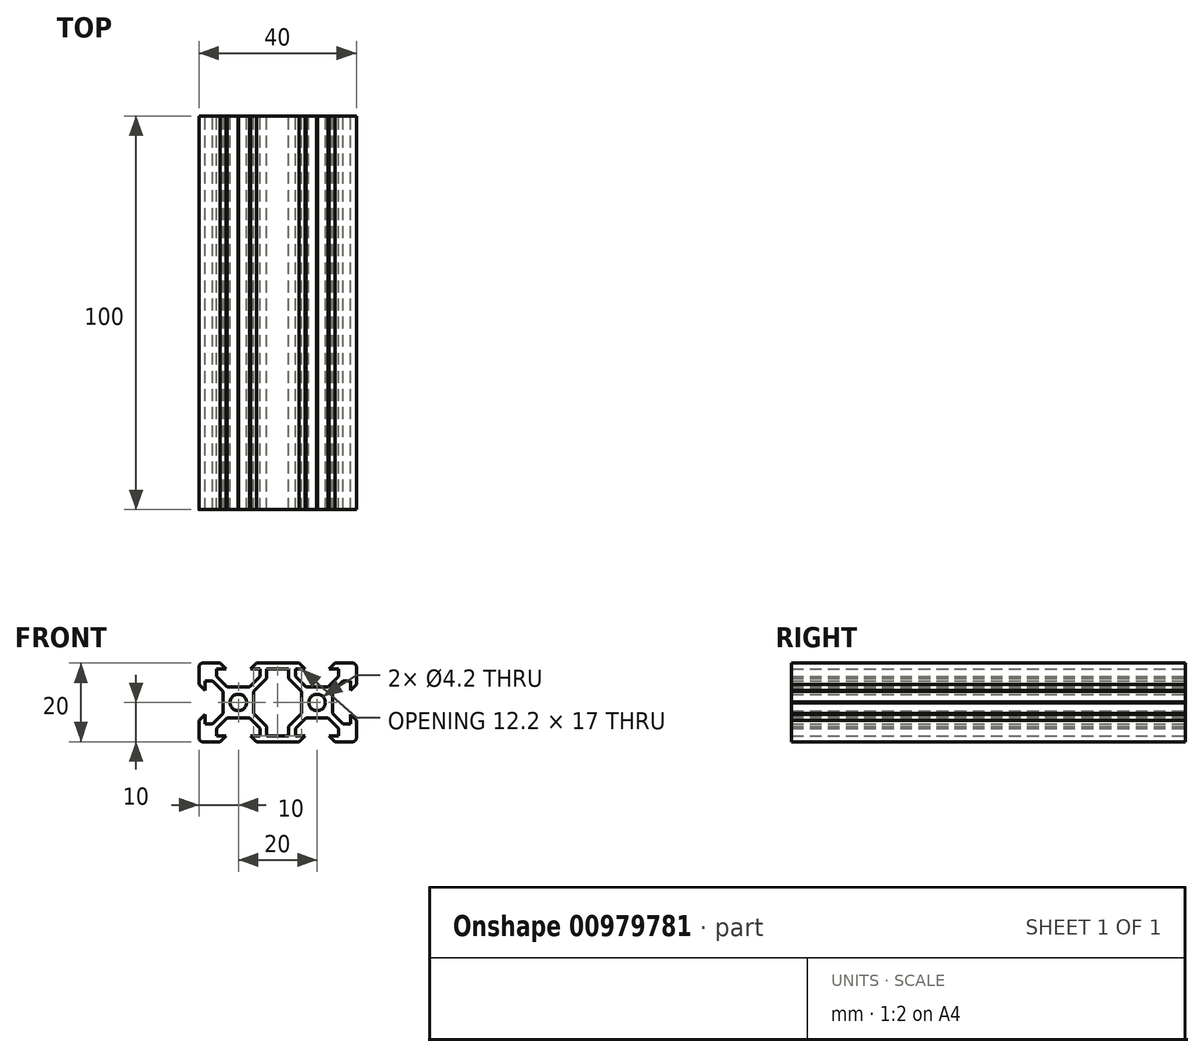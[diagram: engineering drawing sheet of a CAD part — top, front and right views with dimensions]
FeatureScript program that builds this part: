
annotation { "Feature Type Name" : "Feature", "Feature Type Description" : "" }
export const myFeature = defineFeature(function(context is Context, id is Id, definition is map)
    precondition{}
    {
        {
            var Q0;
            Q0=qCreatedBy(makeId("Front.planeOp"),FACE);
            var sketch = newSketch(context, id + "F0", { "sketchPlane" : qUnion([Q0])});
            skLineSegment(sketch, "E0.MirrorCS", {"start": v(-15.5, 8.5) * mm, "end": v(-15.5, 6.56) * mm});
            skLineSegment(sketch, "E1.MirrorCS", {"start": v(-16.56, 5.5) * mm, "end": v(-18.5, 5.5) * mm});
            skLineSegment(sketch, "E2.MirrorCS", {"start": v(-20, 10) * mm, "end": v(-20, 4.6) * mm});
            skLineSegment(sketch, "E3.MirrorCS", {"start": v(-2.8, 6.14) * mm, "end": v(-6.1, 2.84) * mm});
            skLineSegment(sketch, "E4.MirrorCS", {"start": v(-6.1, 2.84) * mm, "end": v(-6.1, 0) * mm});
            skLineSegment(sketch, "E5.MirrorCS", {"start": v(-18.5, 3.1) * mm, "end": v(-20, 4.6) * mm});
            skLineSegment(sketch, "E6.MirrorCS", {"start": v(-15.5, 6.56) * mm, "end": v(-12.84, 3.9) * mm});
            skLineSegment(sketch, "E7.MirrorCS", {"start": v(-13.1, 8.5) * mm, "end": v(-14.6, 10) * mm});
            skLineSegment(sketch, "E8.MirrorCS", {"start": v(-4.5, 8.5) * mm, "end": v(-4.5, 6.56) * mm});
            skLineSegment(sketch, "E9.MirrorCS", {"start": v(-18.5, 5.5) * mm, "end": v(-18.5, 3.1) * mm});
            skLineSegment(sketch, "E10.MirrorCS", {"start": v(-4.5, 6.56) * mm, "end": v(-7.16, 3.9) * mm});
            skLineSegment(sketch, "E11.MirrorCS", {"start": v(-13.9, 2.84) * mm, "end": v(-13.9, 0.1) * mm});
            skLineSegment(sketch, "E12.MirrorCS", {"start": v(-6.9, 8.5) * mm, "end": v(-5.4, 10) * mm});
            skLineSegment(sketch, "E13.MirrorCS", {"start": v(-5.4, 10) * mm, "end": v(0, 10) * mm});
            skLineSegment(sketch, "E14.MirrorCS", {"start": v(-4.5, 8.5) * mm, "end": v(-6.9, 8.5) * mm});
            skLineSegment(sketch, "E15.MirrorCS", {"start": v(-14.6, 10) * mm, "end": v(-20, 10) * mm});
            skLineSegment(sketch, "E16.MirrorCS", {"start": v(-16.56, 5.5) * mm, "end": v(-13.9, 2.84) * mm});
            skLineSegment(sketch, "E17.MirrorCS", {"start": v(-15.5, 8.5) * mm, "end": v(-13.1, 8.5) * mm});
            skLineSegment(sketch, "E18", {"start": v(-2.8, 8.5) * mm, "end": v(-2.8, 6.14) * mm});
            skLineSegment(sketch, "E19", {"start": v(-12.84, 3.9) * mm, "end": v(-10.1, 3.9) * mm});
            skLineSegment(sketch, "E20", {"start": v(-2.8, 8.5) * mm, "end": v(0, 8.5) * mm});
            skLineSegment(sketch, "E21", {"start": v(-12.25, 8.5) * mm, "end": v(-7.9, 8.5) * mm, "construction": true});
            skLineSegment(sketch, "E22", {"start": v(-7.9, 10) * mm, "end": v(-12.25, 10) * mm, "construction": true});
            skArc(sketch, "E23", {"start": v(-7.9, 0) * mm, "mid": v(-10, 2.1) * mm, "end": v(-12.1, 0) * mm});
            skLineSegment(sketch, "E24", {"start": v(-10, 0) * mm, "end": v(-10, 1.07) * mm, "construction": true});
            skLineSegment(sketch, "E25.MirrorCS", {"start": v(-10, 0) * mm, "end": v(-10, -1.07) * mm, "construction": true});
            skLineSegment(sketch, "E26.top", {"start": v(-10.1, 3.7) * mm, "end": v(-9.9, 3.7) * mm});
            skLineSegment(sketch, "E26.left", {"start": v(-10.1, 3.9) * mm, "end": v(-10.1, 3.7) * mm});
            skLineSegment(sketch, "E26.right", {"start": v(-9.9, 3.9) * mm, "end": v(-9.9, 3.7) * mm});
            skLineSegment(sketch, "E27.trimOffspring", {"start": v(-9.9, 3.9) * mm, "end": v(-7.16, 3.9) * mm});
            skLineSegment(sketch, "E28", {"start": v(-13.9, 0.1) * mm, "end": v(-13.7, 0.1) * mm});
            skLineSegment(sketch, "E29", {"start": v(-13.7, 0.1) * mm, "end": v(-13.7, 0) * mm});
            skPoint(sketch, "E30.orphan", {"position": v(-13.9, 0) * mm});
            skLineSegment(sketch, "E31.MirrorCS", {"start": v(13.7, 0.1) * mm, "end": v(13.7, 0) * mm});
            skLineSegment(sketch, "E32.MirrorCS", {"start": v(13.9, 0.1) * mm, "end": v(13.7, 0.1) * mm});
            skLineSegment(sketch, "E33.MirrorCS", {"start": v(10.1, 3.7) * mm, "end": v(9.9, 3.7) * mm});
            skLineSegment(sketch, "E34.MirrorCS", {"start": v(10.1, 3.9) * mm, "end": v(10.1, 3.7) * mm});
            skLineSegment(sketch, "E35.MirrorCS", {"start": v(9.9, 3.9) * mm, "end": v(9.9, 3.7) * mm});
            skLineSegment(sketch, "E36.MirrorCS", {"start": v(20, 10) * mm, "end": v(20, 4.6) * mm});
            skLineSegment(sketch, "E37.MirrorCS", {"start": v(4.5, 6.56) * mm, "end": v(7.16, 3.9) * mm});
            skLineSegment(sketch, "E38.MirrorCS", {"start": v(2.8, 8.5) * mm, "end": v(0, 8.5) * mm});
            skLineSegment(sketch, "E39.MirrorCS", {"start": v(18.5, 5.5) * mm, "end": v(18.5, 3.1) * mm});
            skLineSegment(sketch, "E40.MirrorCS", {"start": v(16.56, 5.5) * mm, "end": v(18.5, 5.5) * mm});
            skLineSegment(sketch, "E41.MirrorCS", {"start": v(15.5, 8.5) * mm, "end": v(15.5, 6.56) * mm});
            skLineSegment(sketch, "E42.MirrorCS", {"start": v(9.9, 3.9) * mm, "end": v(7.16, 3.9) * mm});
            skLineSegment(sketch, "E43.MirrorCS", {"start": v(13.9, 2.84) * mm, "end": v(13.9, 0.1) * mm});
            skLineSegment(sketch, "E44.MirrorCS", {"start": v(15.5, 8.5) * mm, "end": v(13.1, 8.5) * mm});
            skLineSegment(sketch, "E45.MirrorCS", {"start": v(16.56, 5.5) * mm, "end": v(13.9, 2.84) * mm});
            skLineSegment(sketch, "E46.MirrorCS", {"start": v(13.1, 8.5) * mm, "end": v(14.6, 10) * mm});
            skLineSegment(sketch, "E47.MirrorCS", {"start": v(15.5, 6.56) * mm, "end": v(12.84, 3.9) * mm});
            skLineSegment(sketch, "E48.MirrorCS", {"start": v(12.25, 8.5) * mm, "end": v(7.9, 8.5) * mm, "construction": true});
            skLineSegment(sketch, "E49.MirrorCS", {"start": v(12.84, 3.9) * mm, "end": v(10.1, 3.9) * mm});
            skLineSegment(sketch, "E50.MirrorCS", {"start": v(5.4, 10) * mm, "end": v(0, 10) * mm});
            skLineSegment(sketch, "E51.MirrorCS", {"start": v(2.8, 8.5) * mm, "end": v(2.8, 6.14) * mm});
            skLineSegment(sketch, "E52.MirrorCS", {"start": v(4.5, 8.5) * mm, "end": v(4.5, 6.56) * mm});
            skLineSegment(sketch, "E53.MirrorCS", {"start": v(18.5, 3.1) * mm, "end": v(20, 4.6) * mm});
            skPoint(sketch, "E54.MirrorP", {"position": v(13.9, 0) * mm});
            skArc(sketch, "E55.MirrorCS", {"start": v(7.9, 0) * mm, "mid": v(10, 2.1) * mm, "end": v(12.1, 0) * mm});
            skLineSegment(sketch, "E56.MirrorCS", {"start": v(6.1, 2.84) * mm, "end": v(6.1, 0) * mm});
            skLineSegment(sketch, "E57.MirrorCS", {"start": v(14.6, 10) * mm, "end": v(20, 10) * mm});
            skLineSegment(sketch, "E58.MirrorCS", {"start": v(10, 0) * mm, "end": v(10, 1.07) * mm, "construction": true});
            skLineSegment(sketch, "E59.MirrorCS", {"start": v(6.9, 8.5) * mm, "end": v(5.4, 10) * mm});
            skLineSegment(sketch, "E60.MirrorCS", {"start": v(2.8, 6.14) * mm, "end": v(6.1, 2.84) * mm});
            skLineSegment(sketch, "E61.MirrorCS", {"start": v(7.9, 10) * mm, "end": v(12.25, 10) * mm, "construction": true});
            skLineSegment(sketch, "E62.MirrorCS", {"start": v(4.5, 8.5) * mm, "end": v(6.9, 8.5) * mm});
            skLineSegment(sketch, "E63.MirrorCS", {"start": v(13.7, -0.1) * mm, "end": v(13.7, 0) * mm});
            skLineSegment(sketch, "E64.MirrorCS", {"start": v(-13.9, -0.1) * mm, "end": v(-13.7, -0.1) * mm});
            skLineSegment(sketch, "E65.MirrorCS", {"start": v(-13.7, -0.1) * mm, "end": v(-13.7, 0) * mm});
            skLineSegment(sketch, "E66.MirrorCS", {"start": v(13.9, -0.1) * mm, "end": v(13.7, -0.1) * mm});
            skLineSegment(sketch, "E67.MirrorCS", {"start": v(-9.9, -3.9) * mm, "end": v(-9.9, -3.7) * mm});
            skLineSegment(sketch, "E68.MirrorCS", {"start": v(9.9, -3.9) * mm, "end": v(9.9, -3.7) * mm});
            skLineSegment(sketch, "E69.MirrorCS", {"start": v(10.1, -3.9) * mm, "end": v(10.1, -3.7) * mm});
            skLineSegment(sketch, "E70.MirrorCS", {"start": v(10.1, -3.7) * mm, "end": v(9.9, -3.7) * mm});
            skLineSegment(sketch, "E71.MirrorCS", {"start": v(-10.1, -3.7) * mm, "end": v(-9.9, -3.7) * mm});
            skLineSegment(sketch, "E72.MirrorCS", {"start": v(-10.1, -3.9) * mm, "end": v(-10.1, -3.7) * mm});
            skLineSegment(sketch, "E73.MirrorCS", {"start": v(15.5, -6.56) * mm, "end": v(12.84, -3.9) * mm});
            skLineSegment(sketch, "E74.MirrorCS", {"start": v(-18.5, -3.1) * mm, "end": v(-20, -4.6) * mm});
            skLineSegment(sketch, "E75.MirrorCS", {"start": v(2.8, -6.14) * mm, "end": v(6.1, -2.84) * mm});
            skLineSegment(sketch, "E76.MirrorCS", {"start": v(-4.5, -8.5) * mm, "end": v(-6.9, -8.5) * mm});
            skLineSegment(sketch, "E77.MirrorCS", {"start": v(-6.9, -8.5) * mm, "end": v(-5.4, -10) * mm});
            skLineSegment(sketch, "E78.MirrorCS", {"start": v(-15.5, -8.5) * mm, "end": v(-13.1, -8.5) * mm});
            skLineSegment(sketch, "E79.MirrorCS", {"start": v(-12.25, -8.5) * mm, "end": v(-7.9, -8.5) * mm, "construction": true});
            skLineSegment(sketch, "E80.MirrorCS", {"start": v(13.9, -2.84) * mm, "end": v(13.9, -0.1) * mm});
            skLineSegment(sketch, "E81.MirrorCS", {"start": v(-15.5, -8.5) * mm, "end": v(-15.5, -6.56) * mm});
            skLineSegment(sketch, "E82.MirrorCS", {"start": v(-7.9, -10) * mm, "end": v(-12.25, -10) * mm, "construction": true});
            skLineSegment(sketch, "E83.MirrorCS", {"start": v(16.56, -5.5) * mm, "end": v(13.9, -2.84) * mm});
            skArc(sketch, "E84.MirrorCS", {"start": v(-7.9, 0) * mm, "mid": v(-10, -2.1) * mm, "end": v(-12.1, 0) * mm});
            skLineSegment(sketch, "E85.MirrorCS", {"start": v(-2.8, -8.5) * mm, "end": v(-2.8, -6.14) * mm});
            skLineSegment(sketch, "E86.MirrorCS", {"start": v(-16.56, -5.5) * mm, "end": v(-18.5, -5.5) * mm});
            skLineSegment(sketch, "E87.MirrorCS", {"start": v(4.5, -8.5) * mm, "end": v(6.9, -8.5) * mm});
            skLineSegment(sketch, "E88.MirrorCS", {"start": v(14.6, -10) * mm, "end": v(20, -10) * mm});
            skLineSegment(sketch, "E89.MirrorCS", {"start": v(-2.8, -6.14) * mm, "end": v(-6.1, -2.84) * mm});
            skLineSegment(sketch, "E90.MirrorCS", {"start": v(7.9, -10) * mm, "end": v(12.25, -10) * mm, "construction": true});
            skLineSegment(sketch, "E91.MirrorCS", {"start": v(-20, -10) * mm, "end": v(-20, -4.6) * mm});
            skLineSegment(sketch, "E92.MirrorCS", {"start": v(6.9, -8.5) * mm, "end": v(5.4, -10) * mm});
            skLineSegment(sketch, "E93.MirrorCS", {"start": v(4.5, -6.56) * mm, "end": v(7.16, -3.9) * mm});
            skLineSegment(sketch, "E94.MirrorCS", {"start": v(9.9, -3.9) * mm, "end": v(7.16, -3.9) * mm});
            skLineSegment(sketch, "E95.MirrorCS", {"start": v(-12.84, -3.9) * mm, "end": v(-10.1, -3.9) * mm});
            skLineSegment(sketch, "E96.MirrorCS", {"start": v(12.84, -3.9) * mm, "end": v(10.1, -3.9) * mm});
            skLineSegment(sketch, "E97.MirrorCS", {"start": v(-4.5, -6.56) * mm, "end": v(-7.16, -3.9) * mm});
            skLineSegment(sketch, "E98.MirrorCS", {"start": v(20, -10) * mm, "end": v(20, -4.6) * mm});
            skLineSegment(sketch, "E99.MirrorCS", {"start": v(15.5, -8.5) * mm, "end": v(13.1, -8.5) * mm});
            skLineSegment(sketch, "E100.MirrorCS", {"start": v(-13.9, -2.84) * mm, "end": v(-13.9, -0.1) * mm});
            skLineSegment(sketch, "E101.MirrorCS", {"start": v(-5.4, -10) * mm, "end": v(0, -10) * mm});
            skLineSegment(sketch, "E102.MirrorCS", {"start": v(-9.9, -3.9) * mm, "end": v(-7.16, -3.9) * mm});
            skLineSegment(sketch, "E103.MirrorCS", {"start": v(18.5, -5.5) * mm, "end": v(18.5, -3.1) * mm});
            skLineSegment(sketch, "E104.MirrorCS", {"start": v(-2.8, -8.5) * mm, "end": v(0, -8.5) * mm});
            skLineSegment(sketch, "E105.MirrorCS", {"start": v(18.5, -3.1) * mm, "end": v(20, -4.6) * mm});
            skLineSegment(sketch, "E106.MirrorCS", {"start": v(-13.1, -8.5) * mm, "end": v(-14.6, -10) * mm});
            skLineSegment(sketch, "E107.MirrorCS", {"start": v(15.5, -8.5) * mm, "end": v(15.5, -6.56) * mm});
            skLineSegment(sketch, "E108.MirrorCS", {"start": v(-6.1, -2.84) * mm, "end": v(-6.1, 0) * mm});
            skArc(sketch, "E109.MirrorCS", {"start": v(7.9, 0) * mm, "mid": v(10, -2.1) * mm, "end": v(12.1, 0) * mm});
            skLineSegment(sketch, "E110.MirrorCS", {"start": v(10, 0) * mm, "end": v(10, -1.07) * mm, "construction": true});
            skLineSegment(sketch, "E111.MirrorCS", {"start": v(2.8, -8.5) * mm, "end": v(0, -8.5) * mm});
            skLineSegment(sketch, "E112.MirrorCS", {"start": v(6.1, -2.84) * mm, "end": v(6.1, 0) * mm});
            skLineSegment(sketch, "E113.MirrorCS", {"start": v(-16.56, -5.5) * mm, "end": v(-13.9, -2.84) * mm});
            skLineSegment(sketch, "E114.MirrorCS", {"start": v(-18.5, -5.5) * mm, "end": v(-18.5, -3.1) * mm});
            skLineSegment(sketch, "E115.MirrorCS", {"start": v(4.5, -8.5) * mm, "end": v(4.5, -6.56) * mm});
            skLineSegment(sketch, "E116.MirrorCS", {"start": v(-15.5, -6.56) * mm, "end": v(-12.84, -3.9) * mm});
            skLineSegment(sketch, "E117.MirrorCS", {"start": v(5.4, -10) * mm, "end": v(0, -10) * mm});
            skLineSegment(sketch, "E118.MirrorCS", {"start": v(12.25, -8.5) * mm, "end": v(7.9, -8.5) * mm, "construction": true});
            skLineSegment(sketch, "E119.MirrorCS", {"start": v(-4.5, -8.5) * mm, "end": v(-4.5, -6.56) * mm});
            skLineSegment(sketch, "E120.MirrorCS", {"start": v(13.1, -8.5) * mm, "end": v(14.6, -10) * mm});
            skLineSegment(sketch, "E121.MirrorCS", {"start": v(2.8, -8.5) * mm, "end": v(2.8, -6.14) * mm});
            skLineSegment(sketch, "E122.MirrorCS", {"start": v(16.56, -5.5) * mm, "end": v(18.5, -5.5) * mm});
            skLineSegment(sketch, "E123.MirrorCS", {"start": v(-14.6, -10) * mm, "end": v(-20, -10) * mm});
            skSolve(sketch);
        }
        {
            var Q0;
            Q0=makeQuery(id+"F0.imprint","IMPRINT",FACE,{"disambiguationData":[TD([[makeQuery(id+"F0.imprint","IMPRINT",EDGE,{"derivedFrom":sQuery(id+"F0.wireOp",EDGE,"E0.MirrorCS")}),-1.0]])]});
            extrude(context, id + "F1", {"entities" : qUnion([Q0]), "depth" : 100 * mm, "offsetDistance" : 25 * mm, "symmetric" : true});
        }
        {
            var Q0;
            Q0=makeQuery(id+"F1.opExtrude","SWEPT_EDGE",EDGE,{"disambiguationData":[OSD([sQuery(id+"F0.wireOp",EDGE,"E2.MirrorCS"),sQuery(id+"F0.wireOp",EDGE,"E15.MirrorCS")])]});
            var Q1;
            Q1=makeQuery(id+"F1.opExtrude","SWEPT_EDGE",EDGE,{"disambiguationData":[OSD([sQuery(id+"F0.wireOp",EDGE,"E36.MirrorCS"),sQuery(id+"F0.wireOp",EDGE,"E57.MirrorCS")])]});
            var Q2;
            Q2=makeQuery(id+"F1.opExtrude","SWEPT_EDGE",EDGE,{"disambiguationData":[OSD([sQuery(id+"F0.wireOp",EDGE,"E88.MirrorCS"),sQuery(id+"F0.wireOp",EDGE,"E98.MirrorCS")])]});
            var Q3;
            Q3=makeQuery(id+"F1.opExtrude","SWEPT_EDGE",EDGE,{"disambiguationData":[OSD([sQuery(id+"F0.wireOp",EDGE,"E91.MirrorCS"),sQuery(id+"F0.wireOp",EDGE,"E123.MirrorCS")])]});
            fillet(context, id + "F2", {"entities" : qUnion([Q0, Q1, Q2, Q3]), "radius" : 1 * mm, "tangentPropagation" : true, "allowEdgeOverflow" : false});
        }
    });
